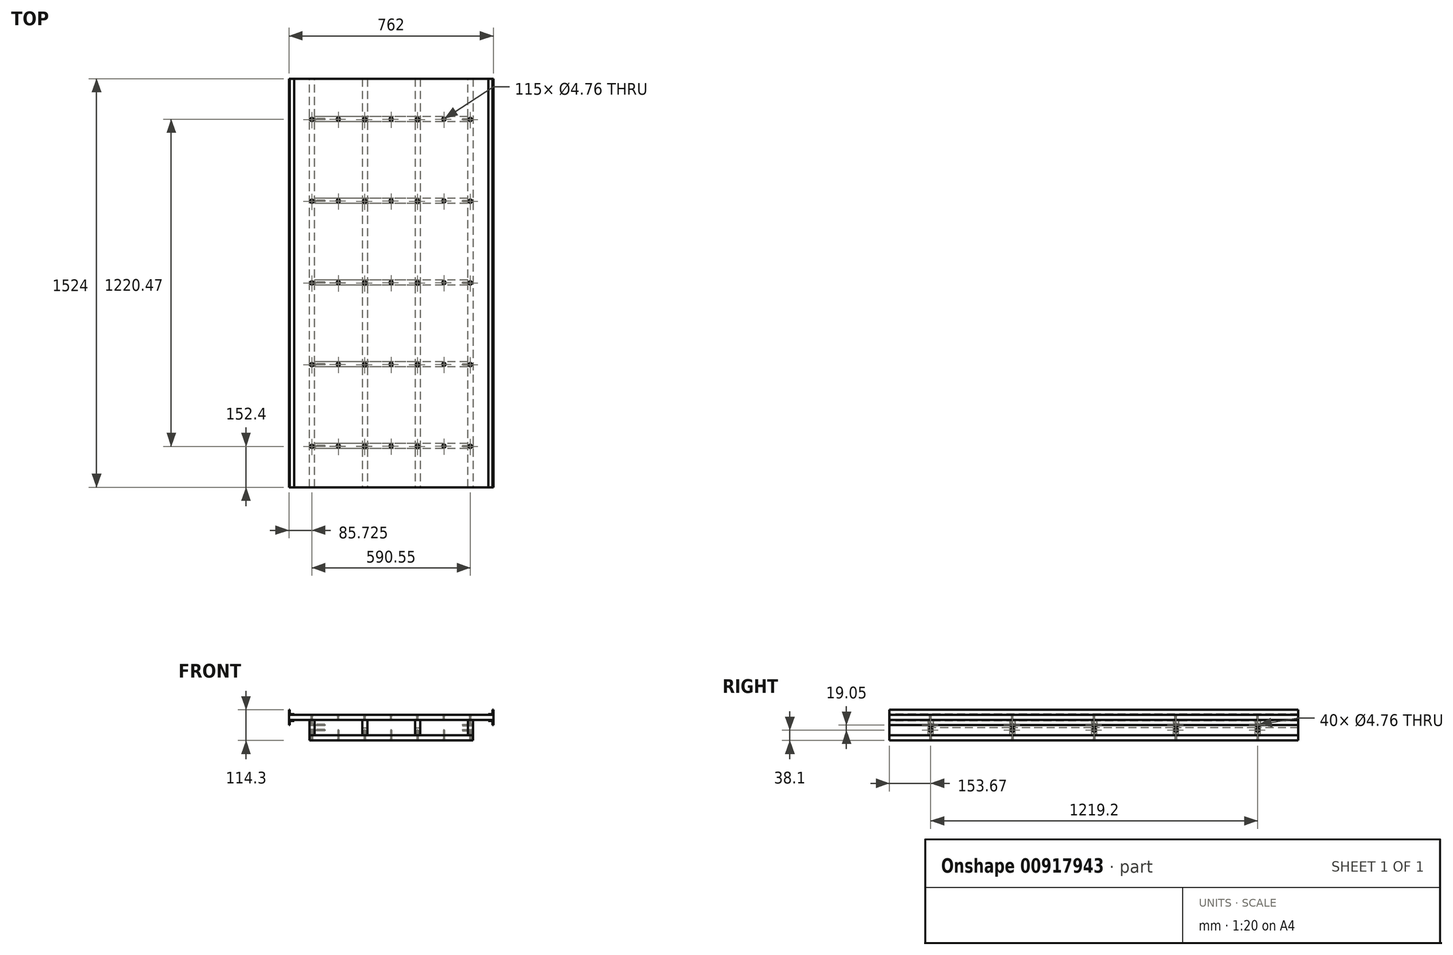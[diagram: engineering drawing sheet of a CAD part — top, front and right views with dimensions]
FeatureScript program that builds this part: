
annotation { "Feature Type Name" : "Feature", "Feature Type Description" : "" }
export const myFeature = defineFeature(function(context is Context, id is Id, definition is map)
    precondition{}
    {
        {
            var Q0;
            Q0=qCreatedBy(makeId("Top.planeOp"),FACE);
            var sketch = newSketch(context, id + "F0", { "sketchPlane" : qUnion([Q0])});
            skLineSegment(sketch, "E0.bottom", {"start": v(0, 1524) * mm, "end": v(762, 1524) * mm});
            skLineSegment(sketch, "E0.top", {"start": v(0, 0) * mm, "end": v(762, 0) * mm});
            skLineSegment(sketch, "E0.left", {"start": v(0, 1524) * mm, "end": v(0, 0) * mm});
            skLineSegment(sketch, "E0.right", {"start": v(762, 1524) * mm, "end": v(762, 0) * mm});
            skSolve(sketch);
        }
        {
            var Q0;
            Q0 = qSketchRegion(id + "F0", true);
            extrude(context, id + "F1", {"entities" : qUnion([Q0]), "oppositeDirection" : true, "depth" : 19.05 * mm, "offsetDistance" : 25.4 * mm});
        }
        {
            var Q0;
            Q0=makeQuery(id+"F1.opExtrude","CAP_FACE",FACE,{"disambiguationData":[OSD([sQuery(id+"F0.wireOp",EDGE,"E0.bottom"),sQuery(id+"F0.wireOp",EDGE,"E0.top"),sQuery(id+"F0.wireOp",EDGE,"E0.left"),sQuery(id+"F0.wireOp",EDGE,"E0.right")])],"isStart":true});
            var sketch = newSketch(context, id + "F2", { "sketchPlane" : qUnion([Q0])});
            skLineSegment(sketch, "E1", {"start": v(85.72, 0) * mm, "end": v(85.72, 1524) * mm, "construction": true});
            skLineSegment(sketch, "E2", {"start": v(76.2, 1524) * mm, "end": v(76.2, 0) * mm});
            skLineSegment(sketch, "E3.MirrorCS", {"start": v(95.25, 1524) * mm, "end": v(95.25, 0) * mm});
            skLineSegment(sketch, "E4", {"start": v(76.2, 1524) * mm, "end": v(95.25, 1524) * mm});
            skLineSegment(sketch, "E5", {"start": v(95.25, 0) * mm, "end": v(76.2, 0) * mm});
            skLineSegment(sketch, "E6.1.0.0", {"start": v(292.1, 1524) * mm, "end": v(292.1, 0) * mm});
            skLineSegment(sketch, "E6.1.0.1", {"start": v(273.05, 1524) * mm, "end": v(273.05, 0) * mm});
            skLineSegment(sketch, "E6.1.0.2", {"start": v(282.57, 0) * mm, "end": v(282.57, 1524) * mm, "construction": true});
            skLineSegment(sketch, "E6.1.0.3", {"start": v(292.1, 0) * mm, "end": v(273.05, 0) * mm});
            skLineSegment(sketch, "E6.1.0.4", {"start": v(273.05, 1524) * mm, "end": v(292.1, 1524) * mm});
            skLineSegment(sketch, "E6.2.0.0", {"start": v(488.95, 1524) * mm, "end": v(488.95, 0) * mm});
            skLineSegment(sketch, "E6.2.0.1", {"start": v(469.9, 1524) * mm, "end": v(469.9, 0) * mm});
            skLineSegment(sketch, "E6.2.0.2", {"start": v(479.42, 0) * mm, "end": v(479.42, 1524) * mm, "construction": true});
            skLineSegment(sketch, "E6.2.0.3", {"start": v(488.95, 0) * mm, "end": v(469.9, 0) * mm});
            skLineSegment(sketch, "E6.2.0.4", {"start": v(469.9, 1524) * mm, "end": v(488.95, 1524) * mm});
            skLineSegment(sketch, "E6.3.0.0", {"start": v(685.8, 1524) * mm, "end": v(685.8, 0) * mm});
            skLineSegment(sketch, "E6.3.0.1", {"start": v(666.75, 1524) * mm, "end": v(666.75, 0) * mm});
            skLineSegment(sketch, "E6.3.0.2", {"start": v(676.27, 0) * mm, "end": v(676.27, 1524) * mm, "construction": true});
            skLineSegment(sketch, "E6.3.0.3", {"start": v(685.8, 0) * mm, "end": v(666.75, 0) * mm});
            skLineSegment(sketch, "E6.3.0.4", {"start": v(666.75, 1524) * mm, "end": v(685.8, 1524) * mm});
            skLineSegment(sketch, "E6.direction1", {"start": v(95.25, 1524) * mm, "end": v(292.1, 1524) * mm, "construction": true});
            skSolve(sketch);
        }
        {
            var Q0;
            Q0=makeQuery(id+"F2.imprint","IMPRINT",FACE,{"disambiguationData":[TD([[makeQuery(id+"F2.imprint","IMPRINT",EDGE,{"derivedFrom":sQuery(id+"F2.wireOp",EDGE,"E2")}),1.0]])]});
            var Q1;
            Q1=makeQuery(id+"F2.imprint","IMPRINT",FACE,{"disambiguationData":[TD([[makeQuery(id+"F2.imprint","IMPRINT",EDGE,{"derivedFrom":sQuery(id+"F2.wireOp",EDGE,"E6.1.0.0")}),-1.0]])]});
            var Q2;
            Q2=makeQuery(id+"F2.imprint","IMPRINT",FACE,{"disambiguationData":[TD([[makeQuery(id+"F2.imprint","IMPRINT",EDGE,{"derivedFrom":sQuery(id+"F2.wireOp",EDGE,"E6.2.0.0")}),-1.0]])]});
            var Q3;
            Q3=makeQuery(id+"F2.imprint","IMPRINT",FACE,{"disambiguationData":[TD([[makeQuery(id+"F2.imprint","IMPRINT",EDGE,{"derivedFrom":sQuery(id+"F2.wireOp",EDGE,"E6.3.0.0")}),-1.0]])]});
            extrude(context, id + "F3", {"entities" : qUnion([Q0, Q1, Q2, Q3]), "oppositeDirection" : true, "depth" : 76.2 * mm, "offsetDistance" : 25.4 * mm, "hasSecondDirection" : true, "secondDirectionBound" : SecondDirectionBoundingType.UP_TO_NEXT, "secondDirectionOppositeDirection" : true, "secondDirectionDepth" : 25.4 * mm});
        }
        {
            var Q0;
            Q0=makeQuery(id+"F1.opExtrude","CAP_FACE",FACE,{"disambiguationData":[OSD([sQuery(id+"F0.wireOp",EDGE,"E0.bottom"),sQuery(id+"F0.wireOp",EDGE,"E0.top"),sQuery(id+"F0.wireOp",EDGE,"E0.left"),sQuery(id+"F0.wireOp",EDGE,"E0.right")])],"isStart":true});
            var sketch = newSketch(context, id + "F4", { "sketchPlane" : qUnion([Q0])});
            skLineSegment(sketch, "E7.bottom", {"start": v(95.25, 163.2) * mm, "end": v(666.75, 163.2) * mm});
            skLineSegment(sketch, "E7.top", {"start": v(95.25, 144.15) * mm, "end": v(666.75, 144.15) * mm});
            skLineSegment(sketch, "E7.left", {"start": v(95.25, 163.2) * mm, "end": v(95.25, 144.15) * mm});
            skLineSegment(sketch, "E7.right", {"start": v(666.75, 163.2) * mm, "end": v(666.75, 144.14) * mm});
            skLineSegment(sketch, "E8.0.1.0", {"start": v(95.25, 468) * mm, "end": v(666.75, 468) * mm});
            skLineSegment(sketch, "E8.0.1.1", {"start": v(95.25, 448.95) * mm, "end": v(666.75, 448.95) * mm});
            skLineSegment(sketch, "E8.0.1.2", {"start": v(95.25, 468) * mm, "end": v(95.25, 448.95) * mm});
            skLineSegment(sketch, "E8.0.1.3", {"start": v(666.75, 468) * mm, "end": v(666.75, 448.94) * mm});
            skLineSegment(sketch, "E8.0.2.0", {"start": v(95.25, 772.8) * mm, "end": v(666.75, 772.8) * mm});
            skLineSegment(sketch, "E8.0.2.1", {"start": v(95.25, 753.75) * mm, "end": v(666.75, 753.75) * mm});
            skLineSegment(sketch, "E8.0.2.2", {"start": v(95.25, 772.8) * mm, "end": v(95.25, 753.75) * mm});
            skLineSegment(sketch, "E8.0.2.3", {"start": v(666.75, 772.8) * mm, "end": v(666.75, 753.75) * mm});
            skLineSegment(sketch, "E8.0.3.0", {"start": v(95.25, 1077.6) * mm, "end": v(666.75, 1077.6) * mm});
            skLineSegment(sketch, "E8.0.3.1", {"start": v(95.25, 1058.55) * mm, "end": v(666.75, 1058.55) * mm});
            skLineSegment(sketch, "E8.0.3.2", {"start": v(95.25, 1077.6) * mm, "end": v(95.25, 1058.55) * mm});
            skLineSegment(sketch, "E8.0.3.3", {"start": v(666.75, 1077.6) * mm, "end": v(666.75, 1058.55) * mm});
            skLineSegment(sketch, "E8.0.4.0", {"start": v(95.25, 1382.4) * mm, "end": v(666.75, 1382.4) * mm});
            skLineSegment(sketch, "E8.0.4.1", {"start": v(95.25, 1363.35) * mm, "end": v(666.75, 1363.35) * mm});
            skLineSegment(sketch, "E8.0.4.2", {"start": v(95.25, 1382.4) * mm, "end": v(95.25, 1363.35) * mm});
            skLineSegment(sketch, "E8.0.4.3", {"start": v(666.75, 1382.4) * mm, "end": v(666.75, 1363.35) * mm});
            skLineSegment(sketch, "E8.direction1", {"start": v(95.25, 144.15) * mm, "end": v(120.65, 144.15) * mm, "construction": true});
            skLineSegment(sketch, "E8.direction2", {"start": v(95.25, 144.15) * mm, "end": v(95.25, 448.95) * mm, "construction": true});
            skSolve(sketch);
        }
        {
            var Q0;
            Q0=makeQuery(id+"F4.imprint","IMPRINT",FACE,{"disambiguationData":[TD([[makeQuery(id+"F4.imprint","IMPRINT",EDGE,{"derivedFrom":sQuery(id+"F4.wireOp",EDGE,"E7.bottom")}),-1.0]])]});
            var Q1;
            Q1=makeQuery(id+"F4.imprint","IMPRINT",FACE,{"disambiguationData":[TD([[makeQuery(id+"F4.imprint","IMPRINT",EDGE,{"derivedFrom":sQuery(id+"F4.wireOp",EDGE,"E8.0.2.0")}),-1.0]])]});
            var Q2;
            Q2=makeQuery(id+"F4.imprint","IMPRINT",FACE,{"disambiguationData":[TD([[makeQuery(id+"F4.imprint","IMPRINT",EDGE,{"derivedFrom":sQuery(id+"F4.wireOp",EDGE,"E8.0.3.0")}),-1.0]])]});
            var Q3;
            Q3=makeQuery(id+"F4.imprint","IMPRINT",FACE,{"disambiguationData":[TD([[makeQuery(id+"F4.imprint","IMPRINT",EDGE,{"derivedFrom":sQuery(id+"F4.wireOp",EDGE,"E8.0.4.0")}),-1.0]])]});
            var Q4;
            Q4=makeQuery(id+"F4.imprint","IMPRINT",FACE,{"disambiguationData":[TD([[makeQuery(id+"F4.imprint","IMPRINT",EDGE,{"derivedFrom":makeQuery(id+"F11.hole-17.boolean.opBoolean","COPY",EDGE,{"derivedFrom":makeQuery(id+"F11.hole-17.opRevolve","SWEPT_EDGE",EDGE,{"disambiguationData":[OSD([sQuery(id+"F11.hole-17.sketch.wireOp",EDGE,"csink_start_line_1"),sQuery(id+"F11.hole-17.sketch.wireOp",EDGE,"csink_start_line_2")])]})})}),1.0]])]});
            var Q5;
            Q5=makeQuery(id+"F4.imprint","IMPRINT",FACE,{"disambiguationData":[TD([[makeQuery(id+"F4.imprint","IMPRINT",EDGE,{"derivedFrom":makeQuery(id+"F11.hole-26.boolean.opBoolean","COPY",EDGE,{"derivedFrom":makeQuery(id+"F11.hole-26.opRevolve","SWEPT_EDGE",EDGE,{"disambiguationData":[OSD([sQuery(id+"F11.hole-26.sketch.wireOp",EDGE,"csink_start_line_1"),sQuery(id+"F11.hole-26.sketch.wireOp",EDGE,"csink_start_line_2")])]})})}),1.0]])]});
            var Q6;
            Q6=makeQuery(id+"F4.imprint","IMPRINT",FACE,{"disambiguationData":[TD([[makeQuery(id+"F4.imprint","IMPRINT",EDGE,{"derivedFrom":sQuery(id+"F4.wireOp",EDGE,"E8.0.1.0")}),-1.0]])]});
            var Q7;
            Q7=makeQuery(id+"F4.imprint","IMPRINT",FACE,{"disambiguationData":[TD([[makeQuery(id+"F4.imprint","IMPRINT",EDGE,{"derivedFrom":makeQuery(id+"F11.hole-20.boolean.opBoolean","COPY",EDGE,{"derivedFrom":makeQuery(id+"F11.hole-20.opRevolve","SWEPT_EDGE",EDGE,{"disambiguationData":[OSD([sQuery(id+"F11.hole-20.sketch.wireOp",EDGE,"csink_start_line_1"),sQuery(id+"F11.hole-20.sketch.wireOp",EDGE,"csink_start_line_2")])]})})}),1.0]])]});
            var Q8;
            Q8=makeQuery(id+"F4.imprint","IMPRINT",FACE,{"disambiguationData":[TD([[makeQuery(id+"F4.imprint","IMPRINT",EDGE,{"derivedFrom":makeQuery(id+"F11.hole-14.boolean.opBoolean","COPY",EDGE,{"derivedFrom":makeQuery(id+"F11.hole-14.opRevolve","SWEPT_EDGE",EDGE,{"disambiguationData":[OSD([sQuery(id+"F11.hole-14.sketch.wireOp",EDGE,"csink_start_line_1"),sQuery(id+"F11.hole-14.sketch.wireOp",EDGE,"csink_start_line_2")])]})})}),1.0]])]});
            var Q9;
            Q9=makeQuery(id+"F4.imprint","IMPRINT",FACE,{"disambiguationData":[TD([[makeQuery(id+"F4.imprint","IMPRINT",EDGE,{"derivedFrom":makeQuery(id+"F11.hole-12.boolean.opBoolean","COPY",EDGE,{"derivedFrom":makeQuery(id+"F11.hole-12.opRevolve","SWEPT_EDGE",EDGE,{"disambiguationData":[OSD([sQuery(id+"F11.hole-12.sketch.wireOp",EDGE,"csink_start_line_1"),sQuery(id+"F11.hole-12.sketch.wireOp",EDGE,"csink_start_line_2")])]})})}),1.0]])]});
            var Q10;
            Q10=makeQuery(id+"F4.imprint","IMPRINT",FACE,{"disambiguationData":[TD([[makeQuery(id+"F4.imprint","IMPRINT",EDGE,{"derivedFrom":makeQuery(id+"F11.hole-16.boolean.opBoolean","COPY",EDGE,{"derivedFrom":makeQuery(id+"F11.hole-16.opRevolve","SWEPT_EDGE",EDGE,{"disambiguationData":[OSD([sQuery(id+"F11.hole-16.sketch.wireOp",EDGE,"csink_start_line_1"),sQuery(id+"F11.hole-16.sketch.wireOp",EDGE,"csink_start_line_2")])]})})}),1.0]])]});
            var Q11;
            Q11=makeQuery(id+"F4.imprint","IMPRINT",FACE,{"disambiguationData":[TD([[makeQuery(id+"F4.imprint","IMPRINT",EDGE,{"derivedFrom":makeQuery(id+"F11.hole-10.boolean.opBoolean","COPY",EDGE,{"derivedFrom":makeQuery(id+"F11.hole-10.opRevolve","SWEPT_EDGE",EDGE,{"disambiguationData":[OSD([sQuery(id+"F11.hole-10.sketch.wireOp",EDGE,"csink_start_line_1"),sQuery(id+"F11.hole-10.sketch.wireOp",EDGE,"csink_start_line_2")])]})})}),1.0]])]});
            var Q12;
            Q12=makeQuery(id+"F4.imprint","IMPRINT",FACE,{"disambiguationData":[TD([[makeQuery(id+"F4.imprint","IMPRINT",EDGE,{"derivedFrom":makeQuery(id+"F11.hole-28.boolean.opBoolean","COPY",EDGE,{"derivedFrom":makeQuery(id+"F11.hole-28.opRevolve","SWEPT_EDGE",EDGE,{"disambiguationData":[OSD([sQuery(id+"F11.hole-28.sketch.wireOp",EDGE,"csink_start_line_1"),sQuery(id+"F11.hole-28.sketch.wireOp",EDGE,"csink_start_line_2")])]})})}),1.0]])]});
            var Q13;
            Q13=makeQuery(id+"F4.imprint","IMPRINT",FACE,{"disambiguationData":[TD([[makeQuery(id+"F4.imprint","IMPRINT",EDGE,{"derivedFrom":makeQuery(id+"F11.hole-8.boolean.opBoolean","COPY",EDGE,{"derivedFrom":makeQuery(id+"F11.hole-8.opRevolve","SWEPT_EDGE",EDGE,{"disambiguationData":[OSD([sQuery(id+"F11.hole-8.sketch.wireOp",EDGE,"csink_start_line_1"),sQuery(id+"F11.hole-8.sketch.wireOp",EDGE,"csink_start_line_2")])]})})}),1.0]])]});
            var Q14;
            Q14=makeQuery(id+"F4.imprint","IMPRINT",FACE,{"disambiguationData":[TD([[makeQuery(id+"F4.imprint","IMPRINT",EDGE,{"derivedFrom":makeQuery(id+"F11.hole-21.boolean.opBoolean","COPY",EDGE,{"derivedFrom":makeQuery(id+"F11.hole-21.opRevolve","SWEPT_EDGE",EDGE,{"disambiguationData":[OSD([sQuery(id+"F11.hole-21.sketch.wireOp",EDGE,"csink_start_line_1"),sQuery(id+"F11.hole-21.sketch.wireOp",EDGE,"csink_start_line_2")])]})})}),1.0]])]});
            var Q15;
            Q15=makeQuery(id+"F3.opExtrude","CAP_FACE",FACE,{"disambiguationData":[OSD([sQuery(id+"F2.wireOp",EDGE,"E6.2.0.0"),sQuery(id+"F2.wireOp",EDGE,"E6.2.0.1"),sQuery(id+"F2.wireOp",EDGE,"E6.2.0.3"),sQuery(id+"F2.wireOp",EDGE,"E6.2.0.4")])],"isStart":false});
            var Q16;
            Q16=makeQuery(id+"F1.opExtrude","CAP_FACE",FACE,{"disambiguationData":[OSD([sQuery(id+"F0.wireOp",EDGE,"E0.bottom"),sQuery(id+"F0.wireOp",EDGE,"E0.top"),sQuery(id+"F0.wireOp",EDGE,"E0.left"),sQuery(id+"F0.wireOp",EDGE,"E0.right")])],"isStart":false});
            extrude(context, id + "F5", {"entities" : qUnion([Q0, Q1, Q2, Q3, Q4, Q5, Q6, Q7, Q8, Q9, Q10, Q11, Q12, Q13, Q14]), "endBound" : BoundingType.UP_TO_SURFACE, "oppositeDirection" : true, "depth" : 25.4 * mm, "endBoundEntityFace" : qUnion([Q15]), "offsetDistance" : 25.4 * mm, "hasSecondDirection" : true, "secondDirectionBound" : SecondDirectionBoundingType.UP_TO_SURFACE, "secondDirectionOppositeDirection" : true, "secondDirectionDepth" : 25.4 * mm, "secondDirectionBoundEntityFace" : qUnion([Q16])});
        }
        {
            var Q0;
            Q0=makeQuery(id+"F5.opExtrude","SWEPT_FACE",FACE,{"disambiguationData":[OSD([sQuery(id+"F4.wireOp",EDGE,"E7.top")])]});
            var sketch = newSketch(context, id + "F6", { "sketchPlane" : qUnion([Q0])});
            skLineSegment(sketch, "E9", {"start": v(95.25, -47.63) * mm, "end": v(666.75, -47.62) * mm, "construction": true});
            skLineSegment(sketch, "E10.bottom", {"start": v(273.05, -19.05) * mm, "end": v(292.1, -19.05) * mm});
            skLineSegment(sketch, "E10.top", {"start": v(273.05, -47.63) * mm, "end": v(292.1, -47.63) * mm});
            skLineSegment(sketch, "E10.left", {"start": v(273.05, -19.05) * mm, "end": v(273.05, -47.63) * mm});
            skLineSegment(sketch, "E10.right", {"start": v(292.1, -19.05) * mm, "end": v(292.1, -47.63) * mm});
            skLineSegment(sketch, "E11.bottom", {"start": v(469.9, -19.05) * mm, "end": v(488.95, -19.05) * mm});
            skLineSegment(sketch, "E11.top", {"start": v(469.9, -47.63) * mm, "end": v(488.95, -47.63) * mm});
            skLineSegment(sketch, "E11.left", {"start": v(469.9, -19.05) * mm, "end": v(469.9, -47.63) * mm});
            skLineSegment(sketch, "E11.right", {"start": v(488.95, -19.05) * mm, "end": v(488.95, -47.63) * mm});
            skSolve(sketch);
        }
        {
            var Q0;
            Q0 = qSketchRegion(id + "F6", true);
            extrude(context, id + "F7", {"entities" : qUnion([Q0]), "operationType" : NewBodyOperationType.REMOVE, "endBound" : BoundingType.THROUGH_ALL, "oppositeDirection" : true, "depth" : 25.4 * mm, "offsetDistance" : 25.4 * mm});
        }
        {
            var Q0;
            Q0=makeQuery(id+"F5.opExtrude","SWEPT_BODY",BODY,{"disambiguationData":[OSD([sQuery(id+"F11.hole-17.sketch.wireOp",EDGE,"csink_start_line_1"),sQuery(id+"F11.hole-17.sketch.wireOp",EDGE,"csink_start_line_2"),sQuery(id+"F11.hole-26.sketch.wireOp",EDGE,"csink_start_line_1"),sQuery(id+"F11.hole-26.sketch.wireOp",EDGE,"csink_start_line_2"),sQuery(id+"F4.wireOp",EDGE,"E7.bottom"),sQuery(id+"F4.wireOp",EDGE,"E7.top"),sQuery(id+"F4.wireOp",EDGE,"E7.left"),sQuery(id+"F4.wireOp",EDGE,"E7.right")])]});
            var Q1;
            Q1=makeQuery(id+"F5.opExtrude","SWEPT_BODY",BODY,{"disambiguationData":[OSD([sQuery(id+"F11.hole-14.sketch.wireOp",EDGE,"csink_start_line_1"),sQuery(id+"F11.hole-14.sketch.wireOp",EDGE,"csink_start_line_2"),sQuery(id+"F11.hole-20.sketch.wireOp",EDGE,"csink_start_line_1"),sQuery(id+"F11.hole-20.sketch.wireOp",EDGE,"csink_start_line_2"),sQuery(id+"F4.wireOp",EDGE,"E8.0.1.0"),sQuery(id+"F4.wireOp",EDGE,"E8.0.1.1"),sQuery(id+"F4.wireOp",EDGE,"E8.0.1.2"),sQuery(id+"F4.wireOp",EDGE,"E8.0.1.3")])]});
            var Q2;
            Q2=makeQuery(id+"F5.opExtrude","SWEPT_BODY",BODY,{"disambiguationData":[OSD([sQuery(id+"F11.hole-12.sketch.wireOp",EDGE,"csink_start_line_1"),sQuery(id+"F11.hole-12.sketch.wireOp",EDGE,"csink_start_line_2"),sQuery(id+"F11.hole-16.sketch.wireOp",EDGE,"csink_start_line_1"),sQuery(id+"F11.hole-16.sketch.wireOp",EDGE,"csink_start_line_2"),sQuery(id+"F4.wireOp",EDGE,"E8.0.2.0"),sQuery(id+"F4.wireOp",EDGE,"E8.0.2.1"),sQuery(id+"F4.wireOp",EDGE,"E8.0.2.2"),sQuery(id+"F4.wireOp",EDGE,"E8.0.2.3")])]});
            var Q3;
            Q3=makeQuery(id+"F5.opExtrude","SWEPT_BODY",BODY,{"disambiguationData":[OSD([sQuery(id+"F11.hole-10.sketch.wireOp",EDGE,"csink_start_line_1"),sQuery(id+"F11.hole-10.sketch.wireOp",EDGE,"csink_start_line_2"),sQuery(id+"F11.hole-28.sketch.wireOp",EDGE,"csink_start_line_1"),sQuery(id+"F11.hole-28.sketch.wireOp",EDGE,"csink_start_line_2"),sQuery(id+"F4.wireOp",EDGE,"E8.0.3.0"),sQuery(id+"F4.wireOp",EDGE,"E8.0.3.1"),sQuery(id+"F4.wireOp",EDGE,"E8.0.3.2"),sQuery(id+"F4.wireOp",EDGE,"E8.0.3.3")])]});
            var Q4;
            Q4=makeQuery(id+"F5.opExtrude","SWEPT_BODY",BODY,{"disambiguationData":[OSD([sQuery(id+"F11.hole-8.sketch.wireOp",EDGE,"csink_start_line_1"),sQuery(id+"F11.hole-8.sketch.wireOp",EDGE,"csink_start_line_2"),sQuery(id+"F11.hole-21.sketch.wireOp",EDGE,"csink_start_line_1"),sQuery(id+"F11.hole-21.sketch.wireOp",EDGE,"csink_start_line_2"),sQuery(id+"F4.wireOp",EDGE,"E8.0.4.0"),sQuery(id+"F4.wireOp",EDGE,"E8.0.4.1"),sQuery(id+"F4.wireOp",EDGE,"E8.0.4.2"),sQuery(id+"F4.wireOp",EDGE,"E8.0.4.3")])]});
            var Q5;
            Q5=makeQuery(id+"F3.opExtrude","SWEPT_BODY",BODY,{"disambiguationData":[OSD([sQuery(id+"F2.wireOp",EDGE,"E6.1.0.0"),sQuery(id+"F2.wireOp",EDGE,"E6.1.0.1"),sQuery(id+"F2.wireOp",EDGE,"E6.1.0.3"),sQuery(id+"F2.wireOp",EDGE,"E6.1.0.4")])]});
            var Q6;
            Q6=makeQuery(id+"F3.opExtrude","SWEPT_BODY",BODY,{"disambiguationData":[OSD([sQuery(id+"F2.wireOp",EDGE,"E6.2.0.0"),sQuery(id+"F2.wireOp",EDGE,"E6.2.0.1"),sQuery(id+"F2.wireOp",EDGE,"E6.2.0.3"),sQuery(id+"F2.wireOp",EDGE,"E6.2.0.4")])]});
            booleanBodies(context, id + "F8", {"operationType" : BooleanOperationType.SUBTRACTION, "tools" : qUnion([Q0, Q1, Q2, Q3, Q4]), "targets" : qUnion([Q5, Q6]), "keepTools" : true});
        }
        {
            var Q0;
            {var subQ0=sQuery(id+"F2.wireOp",EDGE,"E3.MirrorCS");Q0=makeQuery(id+"F2.imprint","IMPRINT",FACE,{"disambiguationData":[TD([[makeQuery(id+"F2.imprint","IMPRINT",EDGE,{"derivedFrom":subQ0}),1.0]])]});}
            var sketch = newSketch(context, id + "F9", { "sketchPlane" : qUnion([Q0])});
            skPoint(sketch, "E12", {"position": v(85.72, 152.4) * mm});
            skPoint(sketch, "E13.0.1.0", {"position": v(85.72, 457.2) * mm});
            skPoint(sketch, "E13.0.2.0", {"position": v(85.72, 762) * mm});
            skPoint(sketch, "E13.0.3.0", {"position": v(85.72, 1066.8) * mm});
            skPoint(sketch, "E13.0.4.0", {"position": v(85.72, 1371.6) * mm});
            skPoint(sketch, "E13.1.0.0", {"position": v(282.57, 152.4) * mm});
            skPoint(sketch, "E13.1.1.0", {"position": v(282.57, 457.2) * mm});
            skPoint(sketch, "E13.1.2.0", {"position": v(282.57, 762) * mm});
            skPoint(sketch, "E13.1.3.0", {"position": v(282.57, 1066.8) * mm});
            skPoint(sketch, "E13.1.4.0", {"position": v(282.57, 1371.6) * mm});
            skPoint(sketch, "E13.2.0.0", {"position": v(479.43, 152.4) * mm});
            skPoint(sketch, "E13.2.1.0", {"position": v(479.43, 457.2) * mm});
            skPoint(sketch, "E13.2.2.0", {"position": v(479.43, 762) * mm});
            skPoint(sketch, "E13.2.3.0", {"position": v(479.43, 1066.8) * mm});
            skPoint(sketch, "E13.2.4.0", {"position": v(479.43, 1371.6) * mm});
            skPoint(sketch, "E13.3.0.0", {"position": v(676.28, 152.4) * mm});
            skPoint(sketch, "E13.3.1.0", {"position": v(676.28, 457.2) * mm});
            skPoint(sketch, "E13.3.2.0", {"position": v(676.28, 762) * mm});
            skPoint(sketch, "E13.3.3.0", {"position": v(676.28, 1066.8) * mm});
            skPoint(sketch, "E13.3.4.0", {"position": v(676.28, 1371.6) * mm});
            skLineSegment(sketch, "E13.direction1", {"start": v(85.72, 152.4) * mm, "end": v(282.57, 152.4) * mm, "construction": true});
            skLineSegment(sketch, "E13.direction2", {"start": v(85.72, 152.4) * mm, "end": v(85.72, 457.2) * mm, "construction": true});
            skSolve(sketch);
        }
        {
            var Q0;
            Q0=makeQuery(id+"F1.opExtrude","CAP_FACE",FACE,{"disambiguationData":[OSD([sQuery(id+"F0.wireOp",EDGE,"E0.bottom"),sQuery(id+"F0.wireOp",EDGE,"E0.top"),sQuery(id+"F0.wireOp",EDGE,"E0.left"),sQuery(id+"F0.wireOp",EDGE,"E0.right")])],"isStart":true});
            var sketch = newSketch(context, id + "F10", { "sketchPlane" : qUnion([Q0])});
            skPoint(sketch, "E14", {"position": v(184.15, 153.67) * mm});
            skLineSegment(sketch, "E15", {"start": v(0, 153.67) * mm, "end": v(762, 153.67) * mm, "construction": true});
            skLineSegment(sketch, "E16", {"start": v(184.15, 0) * mm, "end": v(184.15, 1524) * mm, "construction": true});
            skPoint(sketch, "E17.0.1.0", {"position": v(184.15, 458.47) * mm});
            skPoint(sketch, "E17.0.2.0", {"position": v(184.15, 763.27) * mm});
            skPoint(sketch, "E17.0.3.0", {"position": v(184.15, 1068.07) * mm});
            skPoint(sketch, "E17.0.4.0", {"position": v(184.15, 1372.87) * mm});
            skPoint(sketch, "E17.1.0.0", {"position": v(381, 153.67) * mm});
            skPoint(sketch, "E17.1.1.0", {"position": v(381, 458.47) * mm});
            skPoint(sketch, "E17.1.2.0", {"position": v(381, 763.27) * mm});
            skPoint(sketch, "E17.1.3.0", {"position": v(381, 1068.07) * mm});
            skPoint(sketch, "E17.1.4.0", {"position": v(381, 1372.87) * mm});
            skPoint(sketch, "E17.2.0.0", {"position": v(577.85, 153.67) * mm});
            skPoint(sketch, "E17.2.1.0", {"position": v(577.85, 458.47) * mm});
            skPoint(sketch, "E17.2.2.0", {"position": v(577.85, 763.27) * mm});
            skPoint(sketch, "E17.2.3.0", {"position": v(577.85, 1068.07) * mm});
            skPoint(sketch, "E17.2.4.0", {"position": v(577.85, 1372.87) * mm});
            skLineSegment(sketch, "E17.direction1", {"start": v(184.15, 153.67) * mm, "end": v(381, 153.67) * mm, "construction": true});
            skLineSegment(sketch, "E17.direction2", {"start": v(184.15, 153.67) * mm, "end": v(184.15, 458.47) * mm, "construction": true});
            skSolve(sketch);
        }
        {
            var Q0;
            Q0=sQuery(id+"F9.wireOp",VERTEX,"E13.0.1.0");
            var Q1;
            Q1=sQuery(id+"F9.wireOp",VERTEX,"E13.0.2.0");
            var Q2;
            Q2=sQuery(id+"F9.wireOp",VERTEX,"E13.0.3.0");
            var Q3;
            Q3=sQuery(id+"F9.wireOp",VERTEX,"E13.0.4.0");
            var Q4;
            Q4=sQuery(id+"F9.wireOp",VERTEX,"E13.0.5.0");
            var Q5;
            Q5=sQuery(id+"F9.wireOp",VERTEX,"E13.0.6.0");
            var Q6;
            Q6=sQuery(id+"F9.wireOp",VERTEX,"E13.3.3.0");
            var Q7;
            Q7=sQuery(id+"F9.wireOp",VERTEX,"E13.2.8.0");
            var Q8;
            Q8=sQuery(id+"F9.wireOp",VERTEX,"E13.2.7.0");
            var Q9;
            Q9=sQuery(id+"F9.wireOp",VERTEX,"E13.2.6.0");
            var Q10;
            Q10=sQuery(id+"F9.wireOp",VERTEX,"E13.2.5.0");
            var Q11;
            Q11=sQuery(id+"F9.wireOp",VERTEX,"E13.2.4.0");
            var Q12;
            Q12=sQuery(id+"F9.wireOp",VERTEX,"E13.2.3.0");
            var Q13;
            Q13=sQuery(id+"F9.wireOp",VERTEX,"E13.2.2.0");
            var Q14;
            Q14=sQuery(id+"F9.wireOp",VERTEX,"E13.2.1.0");
            var Q15;
            Q15=sQuery(id+"F9.wireOp",VERTEX,"E13.1.4.0");
            var Q16;
            Q16=sQuery(id+"F9.wireOp",VERTEX,"E13.2.0.0");
            var Q17;
            Q17=sQuery(id+"F9.wireOp",VERTEX,"E13.0.7.0");
            var Q18;
            Q18=sQuery(id+"F9.wireOp",VERTEX,"E13.3.1.0");
            var Q19;
            Q19=sQuery(id+"F9.wireOp",VERTEX,"E13.1.2.0");
            var Q20;
            Q20=sQuery(id+"F9.wireOp",VERTEX,"E13.1.8.0");
            var Q21;
            Q21=sQuery(id+"F9.wireOp",VERTEX,"E13.0.8.0");
            var Q22;
            Q22=sQuery(id+"F9.wireOp",VERTEX,"E13.3.0.0");
            var Q23;
            Q23=sQuery(id+"F9.wireOp",VERTEX,"E13.1.3.0");
            var Q24;
            Q24=sQuery(id+"F9.wireOp",VERTEX,"E13.1.7.0");
            var Q25;
            Q25=sQuery(id+"F9.wireOp",VERTEX,"E13.1.0.0");
            var Q26;
            Q26=sQuery(id+"F9.wireOp",VERTEX,"E13.3.2.0");
            var Q27;
            Q27=sQuery(id+"F9.wireOp",VERTEX,"E13.1.6.0");
            var Q28;
            Q28=sQuery(id+"F9.wireOp",VERTEX,"E13.1.1.0");
            var Q29;
            Q29=sQuery(id+"F9.wireOp",VERTEX,"E13.3.5.0");
            var Q30;
            Q30=sQuery(id+"F9.wireOp",VERTEX,"E13.1.5.0");
            var Q31;
            Q31=sQuery(id+"F9.wireOp",VERTEX,"E13.3.4.0");
            var Q32;
            Q32=sQuery(id+"F9.wireOp",VERTEX,"E13.3.8.0");
            var Q33;
            Q33=sQuery(id+"F9.wireOp",VERTEX,"E13.3.7.0");
            var Q34;
            Q34=sQuery(id+"F9.wireOp",VERTEX,"E13.3.6.0");
            var Q35;
            Q35=sQuery(id+"F9.wireOp",VERTEX,"E12");
            var Q36;
            Q36=sQuery(id+"F10.wireOp",VERTEX,"E17.0.3.0");
            var Q37;
            Q37=sQuery(id+"F10.wireOp",VERTEX,"E17.1.4.0");
            var Q38;
            Q38=sQuery(id+"F10.wireOp",VERTEX,"E17.1.0.0");
            var Q39;
            Q39=sQuery(id+"F10.wireOp",VERTEX,"E17.2.4.0");
            var Q40;
            Q40=sQuery(id+"F10.wireOp",VERTEX,"E17.1.2.0");
            var Q41;
            Q41=sQuery(id+"F10.wireOp",VERTEX,"E17.0.1.0");
            var Q42;
            Q42=sQuery(id+"F10.wireOp",VERTEX,"E17.0.2.0");
            var Q43;
            Q43=sQuery(id+"F10.wireOp",VERTEX,"E17.2.0.0");
            var Q44;
            Q44=sQuery(id+"F10.wireOp",VERTEX,"E17.2.2.0");
            var Q45;
            Q45=sQuery(id+"F10.wireOp",VERTEX,"E17.1.1.0");
            var Q46;
            Q46=sQuery(id+"F10.wireOp",VERTEX,"E14");
            var Q47;
            Q47=sQuery(id+"F10.wireOp",VERTEX,"E17.2.1.0");
            var Q48;
            Q48=sQuery(id+"F10.wireOp",VERTEX,"E17.0.4.0");
            var Q49;
            Q49=sQuery(id+"F10.wireOp",VERTEX,"E17.2.3.0");
            var Q50;
            Q50=sQuery(id+"F10.wireOp",VERTEX,"E17.1.3.0");
            var Q51;
            Q51=makeQuery(id+"F1.opExtrude","SWEPT_BODY",BODY,{"disambiguationData":[OSD([sQuery(id+"F0.wireOp",EDGE,"E0.bottom"),sQuery(id+"F0.wireOp",EDGE,"E0.top"),sQuery(id+"F0.wireOp",EDGE,"E0.left"),sQuery(id+"F0.wireOp",EDGE,"E0.right")])]});
            var Q52;
            Q52=makeQuery(id+"F3.opExtrude","SWEPT_BODY",BODY,{"disambiguationData":[OSD([sQuery(id+"F2.wireOp",EDGE,"E2"),sQuery(id+"F2.wireOp",EDGE,"E3.MirrorCS"),sQuery(id+"F2.wireOp",EDGE,"E4"),sQuery(id+"F2.wireOp",EDGE,"E5")])]});
            var Q53;
            Q53=makeQuery(id+"F3.opExtrude","SWEPT_BODY",BODY,{"disambiguationData":[OSD([sQuery(id+"F2.wireOp",EDGE,"E6.3.0.0"),sQuery(id+"F2.wireOp",EDGE,"E6.3.0.1"),sQuery(id+"F2.wireOp",EDGE,"E6.3.0.3"),sQuery(id+"F2.wireOp",EDGE,"E6.3.0.4")])]});
            var Q54;
            Q54=makeQuery(id+"F3.opExtrude","SWEPT_BODY",BODY,{"disambiguationData":[OSD([sQuery(id+"F2.wireOp",EDGE,"E6.2.0.0"),sQuery(id+"F2.wireOp",EDGE,"E6.2.0.1"),sQuery(id+"F2.wireOp",EDGE,"E6.2.0.3"),sQuery(id+"F2.wireOp",EDGE,"E6.2.0.4")])]});
            var Q55;
            Q55=makeQuery(id+"F3.opExtrude","SWEPT_BODY",BODY,{"disambiguationData":[OSD([sQuery(id+"F2.wireOp",EDGE,"E6.1.0.0"),sQuery(id+"F2.wireOp",EDGE,"E6.1.0.1"),sQuery(id+"F2.wireOp",EDGE,"E6.1.0.3"),sQuery(id+"F2.wireOp",EDGE,"E6.1.0.4")])]});
            hole(context, id + "F11", {"style" : HoleStyle.C_SINK, "endStyle" : HoleEndStyle.BLIND, "holeDiameter" : 4.76 * mm, "cSinkDiameter" : 12.7 * mm, "cSinkAngle" : 90 * degree, "majorDiameter" : 6.35 * mm, "holeDepth" : 38.1 * mm, "isTappedThrough" : true, "tappedDepth" : 12.7 * mm, "tapClearance" : 3, "locations" : qUnion([Q0, Q1, Q2, Q3, Q4, Q5, Q6, Q7, Q8, Q9, Q10, Q11, Q12, Q13, Q14, Q15, Q16, Q17, Q18, Q19, Q20, Q21, Q22, Q23, Q24, Q25, Q26, Q27, Q28, Q29, Q30, Q31, Q32, Q33, Q34, Q35, Q36, Q37, Q38, Q39, Q40, Q41, Q42, Q43, Q44, Q45, Q46, Q47, Q48, Q49, Q50]), "scope" : qUnion([Q51, Q52, Q53, Q54, Q55])});
        }
        {
            var Q0;
            Q0=makeQuery(id+"F3.opExtrude","CAP_FACE",FACE,{"disambiguationData":[OSD([sQuery(id+"F2.wireOp",EDGE,"E6.3.0.0"),sQuery(id+"F2.wireOp",EDGE,"E6.3.0.1"),sQuery(id+"F2.wireOp",EDGE,"E6.3.0.3"),sQuery(id+"F2.wireOp",EDGE,"E6.3.0.4")])],"isStart":false});
            var sketch = newSketch(context, id + "F12", { "sketchPlane" : qUnion([Q0])});
            skLineSegment(sketch, "E18.bottom", {"start": v(685.8, 0) * mm, "end": v(76.2, 0) * mm});
            skLineSegment(sketch, "E18.top", {"start": v(685.8, -1524) * mm, "end": v(76.2, -1524) * mm});
            skLineSegment(sketch, "E18.left", {"start": v(685.8, 0) * mm, "end": v(685.8, -1524) * mm});
            skLineSegment(sketch, "E18.right", {"start": v(76.2, 0) * mm, "end": v(76.2, -1524) * mm});
            skSolve(sketch);
        }
        {
            var Q0;
            Q0 = qSketchRegion(id + "F12", true);
            extrude(context, id + "F13", {"entities" : qUnion([Q0]), "depth" : 19.05 * mm, "offsetDistance" : 25.4 * mm});
        }
        {
            var Q0;
            Q0=makeQuery(id+"F13.opExtrude","CAP_FACE",FACE,{"disambiguationData":[OSD([sQuery(id+"F12.wireOp",EDGE,"E18.bottom"),sQuery(id+"F12.wireOp",EDGE,"E18.top"),sQuery(id+"F12.wireOp",EDGE,"E18.left"),sQuery(id+"F12.wireOp",EDGE,"E18.right")])],"isStart":false});
            var sketch = newSketch(context, id + "F14", { "sketchPlane" : qUnion([Q0])});
            skPoint(sketch, "E19.0", {"position": v(676.28, -152.4) * mm});
            skPoint(sketch, "E19.1", {"position": v(577.85, -153.67) * mm});
            skPoint(sketch, "E19.2", {"position": v(479.43, -152.4) * mm});
            skPoint(sketch, "E19.3", {"position": v(85.72, -152.4) * mm});
            skPoint(sketch, "E19.4", {"position": v(85.72, -457.2) * mm});
            skPoint(sketch, "E19.5", {"position": v(184.15, -458.47) * mm});
            skPoint(sketch, "E19.6", {"position": v(282.57, -457.2) * mm});
            skPoint(sketch, "E19.7", {"position": v(381, -458.47) * mm});
            skPoint(sketch, "E19.8", {"position": v(479.43, -457.2) * mm});
            skPoint(sketch, "E19.9", {"position": v(577.85, -458.47) * mm});
            skPoint(sketch, "E19.10", {"position": v(676.28, -457.2) * mm});
            skPoint(sketch, "E19.11", {"position": v(676.28, -762) * mm});
            skPoint(sketch, "E19.12", {"position": v(577.85, -763.27) * mm});
            skPoint(sketch, "E19.13", {"position": v(479.43, -762) * mm});
            skPoint(sketch, "E19.14", {"position": v(381, -763.27) * mm});
            skPoint(sketch, "E19.15", {"position": v(282.57, -762) * mm});
            skPoint(sketch, "E19.16", {"position": v(85.72, -762) * mm});
            skPoint(sketch, "E19.17", {"position": v(85.72, -1066.8) * mm});
            skPoint(sketch, "E19.18", {"position": v(184.15, -1068.07) * mm});
            skPoint(sketch, "E19.19", {"position": v(282.57, -1066.8) * mm});
            skPoint(sketch, "E19.20", {"position": v(381, -1068.07) * mm});
            skPoint(sketch, "E19.21", {"position": v(479.43, -1066.8) * mm});
            skPoint(sketch, "E19.22", {"position": v(577.85, -1068.07) * mm});
            skPoint(sketch, "E19.23", {"position": v(676.28, -1066.8) * mm});
            skPoint(sketch, "E19.24", {"position": v(676.28, -1371.6) * mm});
            skPoint(sketch, "E19.25", {"position": v(577.85, -1372.87) * mm});
            skPoint(sketch, "E19.26", {"position": v(479.43, -1371.6) * mm});
            skPoint(sketch, "E19.27", {"position": v(381, -1372.87) * mm});
            skPoint(sketch, "E19.28", {"position": v(282.57, -1371.6) * mm});
            skPoint(sketch, "E19.29", {"position": v(184.15, -1372.87) * mm});
            skPoint(sketch, "E19.30", {"position": v(85.72, -1371.6) * mm});
            skPoint(sketch, "E19.31", {"position": v(381, -153.67) * mm});
            skPoint(sketch, "E19.32", {"position": v(282.57, -153.67) * mm});
            skPoint(sketch, "E19.33", {"position": v(184.15, -152.4) * mm});
            skPoint(sketch, "E19.34", {"position": v(184.15, -762) * mm});
            skSolve(sketch);
        }
        {
            var Q0;
            Q0=sQuery(id+"F14.wireOp",VERTEX,"E19.33");
            var Q1;
            Q1=sQuery(id+"F14.wireOp",VERTEX,"E19.7");
            var Q2;
            Q2=sQuery(id+"F14.wireOp",VERTEX,"E19.14");
            var Q3;
            Q3=sQuery(id+"F14.wireOp",VERTEX,"E19.11");
            var Q4;
            Q4=sQuery(id+"F14.wireOp",VERTEX,"E19.5");
            var Q5;
            Q5=sQuery(id+"F14.wireOp",VERTEX,"E19.15");
            var Q6;
            Q6=sQuery(id+"F14.wireOp",VERTEX,"E19.31");
            var Q7;
            Q7=sQuery(id+"F14.wireOp",VERTEX,"E19.13");
            var Q8;
            Q8=sQuery(id+"F14.wireOp",VERTEX,"E19.6");
            var Q9;
            Q9=sQuery(id+"F14.wireOp",VERTEX,"E19.10");
            var Q10;
            Q10=sQuery(id+"F14.wireOp",VERTEX,"E19.8");
            var Q11;
            Q11=sQuery(id+"F14.wireOp",VERTEX,"E19.1");
            var Q12;
            Q12=sQuery(id+"F14.wireOp",VERTEX,"E19.2");
            var Q13;
            Q13=sQuery(id+"F14.wireOp",VERTEX,"E19.0");
            var Q14;
            Q14=sQuery(id+"F14.wireOp",VERTEX,"E19.32");
            var Q15;
            Q15=sQuery(id+"F14.wireOp",VERTEX,"E19.9");
            var Q16;
            Q16=sQuery(id+"F14.wireOp",VERTEX,"E19.12");
            var Q17;
            Q17=sQuery(id+"F14.wireOp",VERTEX,"E19.28");
            var Q18;
            Q18=sQuery(id+"F14.wireOp",VERTEX,"E19.23");
            var Q19;
            Q19=sQuery(id+"F14.wireOp",VERTEX,"E19.17");
            var Q20;
            Q20=sQuery(id+"F14.wireOp",VERTEX,"E19.26");
            var Q21;
            Q21=sQuery(id+"F14.wireOp",VERTEX,"E19.3");
            var Q22;
            Q22=sQuery(id+"F14.wireOp",VERTEX,"E19.21");
            var Q23;
            Q23=sQuery(id+"F14.wireOp",VERTEX,"E19.25");
            var Q24;
            Q24=sQuery(id+"F14.wireOp",VERTEX,"E19.19");
            var Q25;
            Q25=sQuery(id+"F14.wireOp",VERTEX,"E19.20");
            var Q26;
            Q26=sQuery(id+"F14.wireOp",VERTEX,"E19.27");
            var Q27;
            Q27=sQuery(id+"F14.wireOp",VERTEX,"E19.16");
            var Q28;
            Q28=sQuery(id+"F14.wireOp",VERTEX,"E19.22");
            var Q29;
            Q29=sQuery(id+"F14.wireOp",VERTEX,"E19.4");
            var Q30;
            Q30=sQuery(id+"F14.wireOp",VERTEX,"E19.29");
            var Q31;
            Q31=sQuery(id+"F14.wireOp",VERTEX,"E19.30");
            var Q32;
            Q32=sQuery(id+"F14.wireOp",VERTEX,"E19.24");
            var Q33;
            Q33=sQuery(id+"F14.wireOp",VERTEX,"E19.18");
            var Q34;
            Q34=sQuery(id+"F14.wireOp",VERTEX,"E19.34");
            var Q35;
            Q35=makeQuery(id+"F5.opExtrude","SWEPT_BODY",BODY,{"disambiguationData":[OSD([sQuery(id+"F4.wireOp",EDGE,"E7.bottom"),sQuery(id+"F4.wireOp",EDGE,"E7.top"),sQuery(id+"F4.wireOp",EDGE,"E7.left"),sQuery(id+"F4.wireOp",EDGE,"E7.right")])]});
            var Q36;
            Q36=makeQuery(id+"F5.opExtrude","SWEPT_BODY",BODY,{"disambiguationData":[OSD([sQuery(id+"F4.wireOp",EDGE,"E8.0.1.0"),sQuery(id+"F4.wireOp",EDGE,"E8.0.1.1"),sQuery(id+"F4.wireOp",EDGE,"E8.0.1.2"),sQuery(id+"F4.wireOp",EDGE,"E8.0.1.3")])]});
            var Q37;
            Q37=makeQuery(id+"F5.opExtrude","SWEPT_BODY",BODY,{"disambiguationData":[OSD([sQuery(id+"F4.wireOp",EDGE,"E8.0.2.0"),sQuery(id+"F4.wireOp",EDGE,"E8.0.2.1"),sQuery(id+"F4.wireOp",EDGE,"E8.0.2.2"),sQuery(id+"F4.wireOp",EDGE,"E8.0.2.3")])]});
            var Q38;
            Q38=makeQuery(id+"F5.opExtrude","SWEPT_BODY",BODY,{"disambiguationData":[OSD([sQuery(id+"F4.wireOp",EDGE,"E8.0.3.0"),sQuery(id+"F4.wireOp",EDGE,"E8.0.3.1"),sQuery(id+"F4.wireOp",EDGE,"E8.0.3.2"),sQuery(id+"F4.wireOp",EDGE,"E8.0.3.3")])]});
            var Q39;
            Q39=makeQuery(id+"F5.opExtrude","SWEPT_BODY",BODY,{"disambiguationData":[OSD([sQuery(id+"F4.wireOp",EDGE,"E8.0.4.0"),sQuery(id+"F4.wireOp",EDGE,"E8.0.4.1"),sQuery(id+"F4.wireOp",EDGE,"E8.0.4.2"),sQuery(id+"F4.wireOp",EDGE,"E8.0.4.3")])]});
            var Q40;
            Q40=makeQuery(id+"F3.opExtrude","SWEPT_BODY",BODY,{"disambiguationData":[OSD([sQuery(id+"F2.wireOp",EDGE,"E2"),sQuery(id+"F2.wireOp",EDGE,"E3.MirrorCS"),sQuery(id+"F2.wireOp",EDGE,"E4"),sQuery(id+"F2.wireOp",EDGE,"E5")])]});
            var Q41;
            Q41=makeQuery(id+"F3.opExtrude","SWEPT_BODY",BODY,{"disambiguationData":[OSD([sQuery(id+"F2.wireOp",EDGE,"E6.3.0.0"),sQuery(id+"F2.wireOp",EDGE,"E6.3.0.1"),sQuery(id+"F2.wireOp",EDGE,"E6.3.0.3"),sQuery(id+"F2.wireOp",EDGE,"E6.3.0.4")])]});
            var Q42;
            Q42=makeQuery(id+"F13.opExtrude","SWEPT_BODY",BODY,{"disambiguationData":[OSD([sQuery(id+"F12.wireOp",EDGE,"E18.bottom"),sQuery(id+"F12.wireOp",EDGE,"E18.top"),sQuery(id+"F12.wireOp",EDGE,"E18.left"),sQuery(id+"F12.wireOp",EDGE,"E18.right")])]});
            var Q43;
            Q43=makeQuery(id+"F3.opExtrude","SWEPT_BODY",BODY,{"disambiguationData":[OSD([sQuery(id+"F2.wireOp",EDGE,"E6.2.0.0"),sQuery(id+"F2.wireOp",EDGE,"E6.2.0.1"),sQuery(id+"F2.wireOp",EDGE,"E6.2.0.3"),sQuery(id+"F2.wireOp",EDGE,"E6.2.0.4")])]});
            var Q44;
            Q44=makeQuery(id+"F3.opExtrude","SWEPT_BODY",BODY,{"disambiguationData":[OSD([sQuery(id+"F2.wireOp",EDGE,"E6.1.0.0"),sQuery(id+"F2.wireOp",EDGE,"E6.1.0.1"),sQuery(id+"F2.wireOp",EDGE,"E6.1.0.3"),sQuery(id+"F2.wireOp",EDGE,"E6.1.0.4")])]});
            hole(context, id + "F15", {"style" : HoleStyle.C_SINK, "endStyle" : HoleEndStyle.BLIND, "holeDiameter" : 4.76 * mm, "cSinkDiameter" : 12.7 * mm, "cSinkAngle" : 90 * degree, "majorDiameter" : 6.35 * mm, "holeDepth" : 38.1 * mm, "isTappedThrough" : true, "tappedDepth" : 12.7 * mm, "tapClearance" : 3, "locations" : qUnion([Q0, Q1, Q2, Q3, Q4, Q5, Q6, Q7, Q8, Q9, Q10, Q11, Q12, Q13, Q14, Q15, Q16, Q17, Q18, Q19, Q20, Q21, Q22, Q23, Q24, Q25, Q26, Q27, Q28, Q29, Q30, Q31, Q32, Q33, Q34]), "scope" : qUnion([Q35, Q36, Q37, Q38, Q39, Q40, Q41, Q42, Q43, Q44])});
        }
        {
            var Q0;
            Q0=makeQuery(id+"F3.opExtrude","SWEPT_FACE",FACE,{"disambiguationData":[OSD([sQuery(id+"F2.wireOp",EDGE,"E2")])]});
            var sketch = newSketch(context, id + "F16", { "sketchPlane" : qUnion([Q0])});
            skLineSegment(sketch, "E20.0", {"start": v(-1382.4, -76.2) * mm, "end": v(-1382.4, -19.05) * mm, "construction": true});
            skLineSegment(sketch, "E20.1", {"start": v(-1363.35, -76.2) * mm, "end": v(-1363.35, -19.05) * mm, "construction": true});
            skLineSegment(sketch, "E20.2", {"start": v(-1077.6, -76.2) * mm, "end": v(-1077.6, -19.05) * mm, "construction": true});
            skLineSegment(sketch, "E20.3", {"start": v(-1058.55, -76.2) * mm, "end": v(-1058.55, -19.05) * mm, "construction": true});
            skLineSegment(sketch, "E20.4", {"start": v(-772.8, -76.2) * mm, "end": v(-772.8, -19.05) * mm, "construction": true});
            skLineSegment(sketch, "E20.5", {"start": v(-753.75, -76.2) * mm, "end": v(-753.75, -19.05) * mm, "construction": true});
            skLineSegment(sketch, "E20.6", {"start": v(-468, -76.2) * mm, "end": v(-468, -19.05) * mm, "construction": true});
            skLineSegment(sketch, "E20.7", {"start": v(-448.95, -76.2) * mm, "end": v(-448.95, -19.05) * mm, "construction": true});
            skLineSegment(sketch, "E20.8", {"start": v(-163.2, -76.2) * mm, "end": v(-163.2, -19.05) * mm, "construction": true});
            skLineSegment(sketch, "E20.9", {"start": v(-144.15, -76.2) * mm, "end": v(-144.15, -19.05) * mm, "construction": true});
            skLineSegment(sketch, "E21", {"start": v(-1372.87, -76.2) * mm, "end": v(-1372.87, -19.05) * mm, "construction": true});
            skLineSegment(sketch, "E22", {"start": v(-1068.07, -76.2) * mm, "end": v(-1068.07, -19.05) * mm, "construction": true});
            skLineSegment(sketch, "E23", {"start": v(-763.27, -76.2) * mm, "end": v(-763.27, -19.05) * mm, "construction": true});
            skLineSegment(sketch, "E24", {"start": v(-458.47, -76.2) * mm, "end": v(-458.47, -19.05) * mm, "construction": true});
            skLineSegment(sketch, "E25", {"start": v(-153.67, -76.2) * mm, "end": v(-153.67, -19.05) * mm, "construction": true});
            skPoint(sketch, "E26", {"position": v(-1372.87, -57.15) * mm});
            skPoint(sketch, "E27", {"position": v(-1372.87, -38.1) * mm});
            skPoint(sketch, "E28.1.0.0", {"position": v(-1068.07, -57.15) * mm});
            skPoint(sketch, "E28.1.0.1", {"position": v(-1068.07, -38.1) * mm});
            skPoint(sketch, "E28.2.0.0", {"position": v(-763.27, -57.15) * mm});
            skPoint(sketch, "E28.2.0.1", {"position": v(-763.27, -38.1) * mm});
            skPoint(sketch, "E28.3.0.0", {"position": v(-458.47, -57.15) * mm});
            skPoint(sketch, "E28.3.0.1", {"position": v(-458.47, -38.1) * mm});
            skPoint(sketch, "E28.4.0.0", {"position": v(-153.67, -57.15) * mm});
            skPoint(sketch, "E28.4.0.1", {"position": v(-153.67, -38.1) * mm});
            skLineSegment(sketch, "E28.direction1", {"start": v(-1372.87, -57.15) * mm, "end": v(-1068.07, -57.15) * mm, "construction": true});
            skSolve(sketch);
        }
        {
            var Q0;
            Q0=sQuery(id+"F16.wireOp",VERTEX,"E28.3.0.0");
            var Q1;
            Q1=sQuery(id+"F16.wireOp",VERTEX,"E27");
            var Q2;
            Q2=sQuery(id+"F16.wireOp",VERTEX,"E26");
            var Q3;
            Q3=sQuery(id+"F16.wireOp",VERTEX,"E28.3.0.1");
            var Q4;
            Q4=sQuery(id+"F16.wireOp",VERTEX,"E28.1.0.0");
            var Q5;
            Q5=sQuery(id+"F16.wireOp",VERTEX,"E28.2.0.1");
            var Q6;
            Q6=sQuery(id+"F16.wireOp",VERTEX,"E28.4.0.0");
            var Q7;
            Q7=sQuery(id+"F16.wireOp",VERTEX,"E28.1.0.1");
            var Q8;
            Q8=sQuery(id+"F16.wireOp",VERTEX,"E28.2.0.0");
            var Q9;
            Q9=sQuery(id+"F16.wireOp",VERTEX,"E28.4.0.1");
            var Q10;
            Q10=makeQuery(id+"F5.opExtrude","SWEPT_BODY",BODY,{"disambiguationData":[OSD([sQuery(id+"F4.wireOp",EDGE,"E7.bottom"),sQuery(id+"F4.wireOp",EDGE,"E7.top"),sQuery(id+"F4.wireOp",EDGE,"E7.left"),sQuery(id+"F4.wireOp",EDGE,"E7.right")])]});
            var Q11;
            Q11=makeQuery(id+"F5.opExtrude","SWEPT_BODY",BODY,{"disambiguationData":[OSD([sQuery(id+"F4.wireOp",EDGE,"E8.0.1.0"),sQuery(id+"F4.wireOp",EDGE,"E8.0.1.1"),sQuery(id+"F4.wireOp",EDGE,"E8.0.1.2"),sQuery(id+"F4.wireOp",EDGE,"E8.0.1.3")])]});
            var Q12;
            Q12=makeQuery(id+"F5.opExtrude","SWEPT_BODY",BODY,{"disambiguationData":[OSD([sQuery(id+"F4.wireOp",EDGE,"E8.0.2.0"),sQuery(id+"F4.wireOp",EDGE,"E8.0.2.1"),sQuery(id+"F4.wireOp",EDGE,"E8.0.2.2"),sQuery(id+"F4.wireOp",EDGE,"E8.0.2.3")])]});
            var Q13;
            Q13=makeQuery(id+"F5.opExtrude","SWEPT_BODY",BODY,{"disambiguationData":[OSD([sQuery(id+"F4.wireOp",EDGE,"E8.0.3.0"),sQuery(id+"F4.wireOp",EDGE,"E8.0.3.1"),sQuery(id+"F4.wireOp",EDGE,"E8.0.3.2"),sQuery(id+"F4.wireOp",EDGE,"E8.0.3.3")])]});
            var Q14;
            Q14=makeQuery(id+"F5.opExtrude","SWEPT_BODY",BODY,{"disambiguationData":[OSD([sQuery(id+"F4.wireOp",EDGE,"E8.0.4.0"),sQuery(id+"F4.wireOp",EDGE,"E8.0.4.1"),sQuery(id+"F4.wireOp",EDGE,"E8.0.4.2"),sQuery(id+"F4.wireOp",EDGE,"E8.0.4.3")])]});
            var Q15;
            Q15=makeQuery(id+"F3.opExtrude","SWEPT_BODY",BODY,{"disambiguationData":[OSD([sQuery(id+"F2.wireOp",EDGE,"E2"),sQuery(id+"F2.wireOp",EDGE,"E3.MirrorCS"),sQuery(id+"F2.wireOp",EDGE,"E4"),sQuery(id+"F2.wireOp",EDGE,"E5")])]});
            hole(context, id + "F17", {"style" : HoleStyle.C_SINK, "endStyle" : HoleEndStyle.BLIND, "holeDiameter" : 4.76 * mm, "cSinkDiameter" : 12.7 * mm, "cSinkAngle" : 90 * degree, "majorDiameter" : 6.35 * mm, "holeDepth" : 38.1 * mm, "isTappedThrough" : true, "tappedDepth" : 12.7 * mm, "tapClearance" : 3, "locations" : qUnion([Q0, Q1, Q2, Q3, Q4, Q5, Q6, Q7, Q8, Q9]), "scope" : qUnion([Q10, Q11, Q12, Q13, Q14, Q15])});
        }
        {
            var Q0;
            Q0=makeQuery(id+"F3.opExtrude","SWEPT_FACE",FACE,{"disambiguationData":[OSD([sQuery(id+"F2.wireOp",EDGE,"E6.3.0.0")])]});
            var sketch = newSketch(context, id + "F18", { "sketchPlane" : qUnion([Q0])});
            skPoint(sketch, "E29.0", {"position": v(1372.87, -38.1) * mm});
            skPoint(sketch, "E29.1", {"position": v(1372.87, -57.15) * mm});
            skPoint(sketch, "E29.2", {"position": v(1068.07, -57.15) * mm});
            skPoint(sketch, "E29.3", {"position": v(1068.07, -38.1) * mm});
            skPoint(sketch, "E29.4", {"position": v(763.27, -38.1) * mm});
            skPoint(sketch, "E29.5", {"position": v(763.27, -57.15) * mm});
            skPoint(sketch, "E29.6", {"position": v(458.47, -57.15) * mm});
            skPoint(sketch, "E29.7", {"position": v(458.47, -38.1) * mm});
            skPoint(sketch, "E29.8", {"position": v(153.67, -57.15) * mm});
            skPoint(sketch, "E29.9", {"position": v(153.67, -38.1) * mm});
            skSolve(sketch);
        }
        {
            var Q0;
            Q0=sQuery(id+"F16.wireOp",VERTEX,"E28.3.0.0");
            var Q1;
            Q1=sQuery(id+"F16.wireOp",VERTEX,"E27");
            var Q2;
            Q2=sQuery(id+"F16.wireOp",VERTEX,"E26");
            var Q3;
            Q3=sQuery(id+"F16.wireOp",VERTEX,"E28.3.0.1");
            var Q4;
            Q4=sQuery(id+"F16.wireOp",VERTEX,"E28.1.0.0");
            var Q5;
            Q5=sQuery(id+"F16.wireOp",VERTEX,"E28.2.0.1");
            var Q6;
            Q6=sQuery(id+"F16.wireOp",VERTEX,"E28.4.0.0");
            var Q7;
            Q7=sQuery(id+"F16.wireOp",VERTEX,"E28.1.0.1");
            var Q8;
            Q8=sQuery(id+"F16.wireOp",VERTEX,"E28.2.0.0");
            var Q9;
            Q9=sQuery(id+"F16.wireOp",VERTEX,"E28.4.0.1");
            var Q10;
            Q10=sQuery(id+"F18.wireOp",VERTEX,"E29.4");
            var Q11;
            Q11=sQuery(id+"F18.wireOp",VERTEX,"E29.7");
            var Q12;
            Q12=sQuery(id+"F18.wireOp",VERTEX,"E29.8");
            var Q13;
            Q13=sQuery(id+"F18.wireOp",VERTEX,"E29.2");
            var Q14;
            Q14=sQuery(id+"F18.wireOp",VERTEX,"E29.9");
            var Q15;
            Q15=sQuery(id+"F18.wireOp",VERTEX,"E29.6");
            var Q16;
            Q16=sQuery(id+"F18.wireOp",VERTEX,"E29.0");
            var Q17;
            Q17=sQuery(id+"F18.wireOp",VERTEX,"E29.1");
            var Q18;
            Q18=sQuery(id+"F18.wireOp",VERTEX,"E29.3");
            var Q19;
            Q19=sQuery(id+"F18.wireOp",VERTEX,"E29.5");
            var Q20;
            Q20=makeQuery(id+"F5.opExtrude","SWEPT_BODY",BODY,{"disambiguationData":[OSD([sQuery(id+"F4.wireOp",EDGE,"E7.bottom"),sQuery(id+"F4.wireOp",EDGE,"E7.top"),sQuery(id+"F4.wireOp",EDGE,"E7.left"),sQuery(id+"F4.wireOp",EDGE,"E7.right")])]});
            var Q21;
            Q21=makeQuery(id+"F5.opExtrude","SWEPT_BODY",BODY,{"disambiguationData":[OSD([sQuery(id+"F4.wireOp",EDGE,"E8.0.1.0"),sQuery(id+"F4.wireOp",EDGE,"E8.0.1.1"),sQuery(id+"F4.wireOp",EDGE,"E8.0.1.2"),sQuery(id+"F4.wireOp",EDGE,"E8.0.1.3")])]});
            var Q22;
            Q22=makeQuery(id+"F5.opExtrude","SWEPT_BODY",BODY,{"disambiguationData":[OSD([sQuery(id+"F4.wireOp",EDGE,"E8.0.2.0"),sQuery(id+"F4.wireOp",EDGE,"E8.0.2.1"),sQuery(id+"F4.wireOp",EDGE,"E8.0.2.2"),sQuery(id+"F4.wireOp",EDGE,"E8.0.2.3")])]});
            var Q23;
            Q23=makeQuery(id+"F5.opExtrude","SWEPT_BODY",BODY,{"disambiguationData":[OSD([sQuery(id+"F4.wireOp",EDGE,"E8.0.3.0"),sQuery(id+"F4.wireOp",EDGE,"E8.0.3.1"),sQuery(id+"F4.wireOp",EDGE,"E8.0.3.2"),sQuery(id+"F4.wireOp",EDGE,"E8.0.3.3")])]});
            var Q24;
            Q24=makeQuery(id+"F5.opExtrude","SWEPT_BODY",BODY,{"disambiguationData":[OSD([sQuery(id+"F4.wireOp",EDGE,"E8.0.4.0"),sQuery(id+"F4.wireOp",EDGE,"E8.0.4.1"),sQuery(id+"F4.wireOp",EDGE,"E8.0.4.2"),sQuery(id+"F4.wireOp",EDGE,"E8.0.4.3")])]});
            var Q25;
            Q25=makeQuery(id+"F3.opExtrude","SWEPT_BODY",BODY,{"disambiguationData":[OSD([sQuery(id+"F2.wireOp",EDGE,"E6.3.0.0"),sQuery(id+"F2.wireOp",EDGE,"E6.3.0.1"),sQuery(id+"F2.wireOp",EDGE,"E6.3.0.3"),sQuery(id+"F2.wireOp",EDGE,"E6.3.0.4")])]});
            hole(context, id + "F19", {"style" : HoleStyle.C_SINK, "endStyle" : HoleEndStyle.BLIND, "holeDiameter" : 4.76 * mm, "cSinkDiameter" : 12.7 * mm, "cSinkAngle" : 90 * degree, "majorDiameter" : 6.35 * mm, "holeDepth" : 38.1 * mm, "isTappedThrough" : true, "tappedDepth" : 12.7 * mm, "tapClearance" : 3, "locations" : qUnion([Q0, Q1, Q2, Q3, Q4, Q5, Q6, Q7, Q8, Q9, Q10, Q11, Q12, Q13, Q14, Q15, Q16, Q17, Q18, Q19]), "scope" : qUnion([Q20, Q21, Q22, Q23, Q24, Q25])});
        }
        {
            var Q0;
            Q0=makeQuery(id+"F1.opExtrude","SWEPT_FACE",FACE,{"disambiguationData":[OSD([sQuery(id+"F0.wireOp",EDGE,"E0.top")])]});
            var sketch = newSketch(context, id + "F20", { "sketchPlane" : qUnion([Q0])});
            skLineSegment(sketch, "E30", {"start": v(742.95, 0) * mm, "end": v(742.95, 3.18) * mm});
            skLineSegment(sketch, "E31", {"start": v(742.95, 3.18) * mm, "end": v(758.82, 3.18) * mm});
            skLineSegment(sketch, "E32", {"start": v(758.82, 3.18) * mm, "end": v(758.82, 19.05) * mm});
            skLineSegment(sketch, "E33", {"start": v(758.82, 19.05) * mm, "end": v(762, 19.05) * mm});
            skLineSegment(sketch, "E34", {"start": v(762, 19.05) * mm, "end": v(762, 0) * mm});
            skLineSegment(sketch, "E35", {"start": v(762, 0) * mm, "end": v(742.95, 0) * mm});
            skLineSegment(sketch, "E36", {"start": v(0, -9.53) * mm, "end": v(762, -9.53) * mm, "construction": true});
            skLineSegment(sketch, "E37", {"start": v(381, -19.05) * mm, "end": v(381, 0) * mm, "construction": true});
            skLineSegment(sketch, "E38.MirrorCS", {"start": v(758.82, -38.1) * mm, "end": v(762, -38.1) * mm});
            skLineSegment(sketch, "E39.MirrorCS", {"start": v(742.95, -19.05) * mm, "end": v(742.95, -22.23) * mm});
            skLineSegment(sketch, "E40.MirrorCS", {"start": v(742.95, -22.23) * mm, "end": v(758.82, -22.23) * mm});
            skLineSegment(sketch, "E41.MirrorCS", {"start": v(758.82, -22.23) * mm, "end": v(758.82, -38.1) * mm});
            skLineSegment(sketch, "E42.MirrorCS", {"start": v(762, -19.05) * mm, "end": v(742.95, -19.05) * mm});
            skLineSegment(sketch, "E43.MirrorCS", {"start": v(762, -38.1) * mm, "end": v(762, -19.05) * mm});
            skLineSegment(sketch, "E44.MirrorCS", {"start": v(381, 0) * mm, "end": v(381, -19.05) * mm, "construction": true});
            skLineSegment(sketch, "E45.MirrorCS", {"start": v(3.18, -38.1) * mm, "end": v(0, -38.1) * mm});
            skLineSegment(sketch, "E46.MirrorCS", {"start": v(0, -38.1) * mm, "end": v(0, -19.05) * mm});
            skLineSegment(sketch, "E47.MirrorCS", {"start": v(0, -19.05) * mm, "end": v(19.05, -19.05) * mm});
            skLineSegment(sketch, "E48.MirrorCS", {"start": v(3.18, -22.23) * mm, "end": v(3.18, -38.1) * mm});
            skLineSegment(sketch, "E49.MirrorCS", {"start": v(0, 19.05) * mm, "end": v(0, 0) * mm});
            skLineSegment(sketch, "E50.MirrorCS", {"start": v(3.18, 19.05) * mm, "end": v(0, 19.05) * mm});
            skLineSegment(sketch, "E51.MirrorCS", {"start": v(19.05, -19.05) * mm, "end": v(19.05, -22.23) * mm});
            skLineSegment(sketch, "E52.MirrorCS", {"start": v(3.18, 3.18) * mm, "end": v(3.18, 19.05) * mm});
            skLineSegment(sketch, "E53.MirrorCS", {"start": v(19.05, 3.18) * mm, "end": v(3.18, 3.18) * mm});
            skLineSegment(sketch, "E54.MirrorCS", {"start": v(19.05, 0) * mm, "end": v(19.05, 3.18) * mm});
            skLineSegment(sketch, "E55.MirrorCS", {"start": v(0, 0) * mm, "end": v(19.05, 0) * mm});
            skLineSegment(sketch, "E56.MirrorCS", {"start": v(19.05, -22.23) * mm, "end": v(3.18, -22.23) * mm});
            skSolve(sketch);
        }
        {
            var Q0;
            Q0=makeQuery(id+"F20.imprint","IMPRINT",FACE,{"disambiguationData":[TD([[makeQuery(id+"F20.imprint","IMPRINT",EDGE,{"derivedFrom":sQuery(id+"F20.wireOp",EDGE,"E30")}),-1.0]])]});
            var Q1;
            Q1=makeQuery(id+"F20.imprint","IMPRINT",FACE,{"disambiguationData":[TD([[makeQuery(id+"F20.imprint","IMPRINT",EDGE,{"derivedFrom":sQuery(id+"F20.wireOp",EDGE,"E39.MirrorCS")}),1.0]])]});
            var Q2;
            Q2=makeQuery(id+"F20.imprint","IMPRINT",FACE,{"disambiguationData":[TD([[makeQuery(id+"F20.imprint","IMPRINT",EDGE,{"derivedFrom":sQuery(id+"F20.wireOp",EDGE,"E45.MirrorCS")}),-1.0]])]});
            var Q3;
            Q3=makeQuery(id+"F20.imprint","IMPRINT",FACE,{"disambiguationData":[TD([[makeQuery(id+"F20.imprint","IMPRINT",EDGE,{"derivedFrom":sQuery(id+"F20.wireOp",EDGE,"E55.MirrorCS")}),1.0]])]});
            var Q4;
            Q4=makeQuery(id+"F1.opExtrude","SWEPT_FACE",FACE,{"disambiguationData":[OSD([sQuery(id+"F0.wireOp",EDGE,"E0.bottom")])]});
            extrude(context, id + "F21", {"entities" : qUnion([Q0, Q1, Q2, Q3]), "endBound" : BoundingType.UP_TO_SURFACE, "oppositeDirection" : true, "depth" : 25.4 * mm, "endBoundEntityFace" : qUnion([Q4]), "offsetDistance" : 25.4 * mm});
        }
    });
